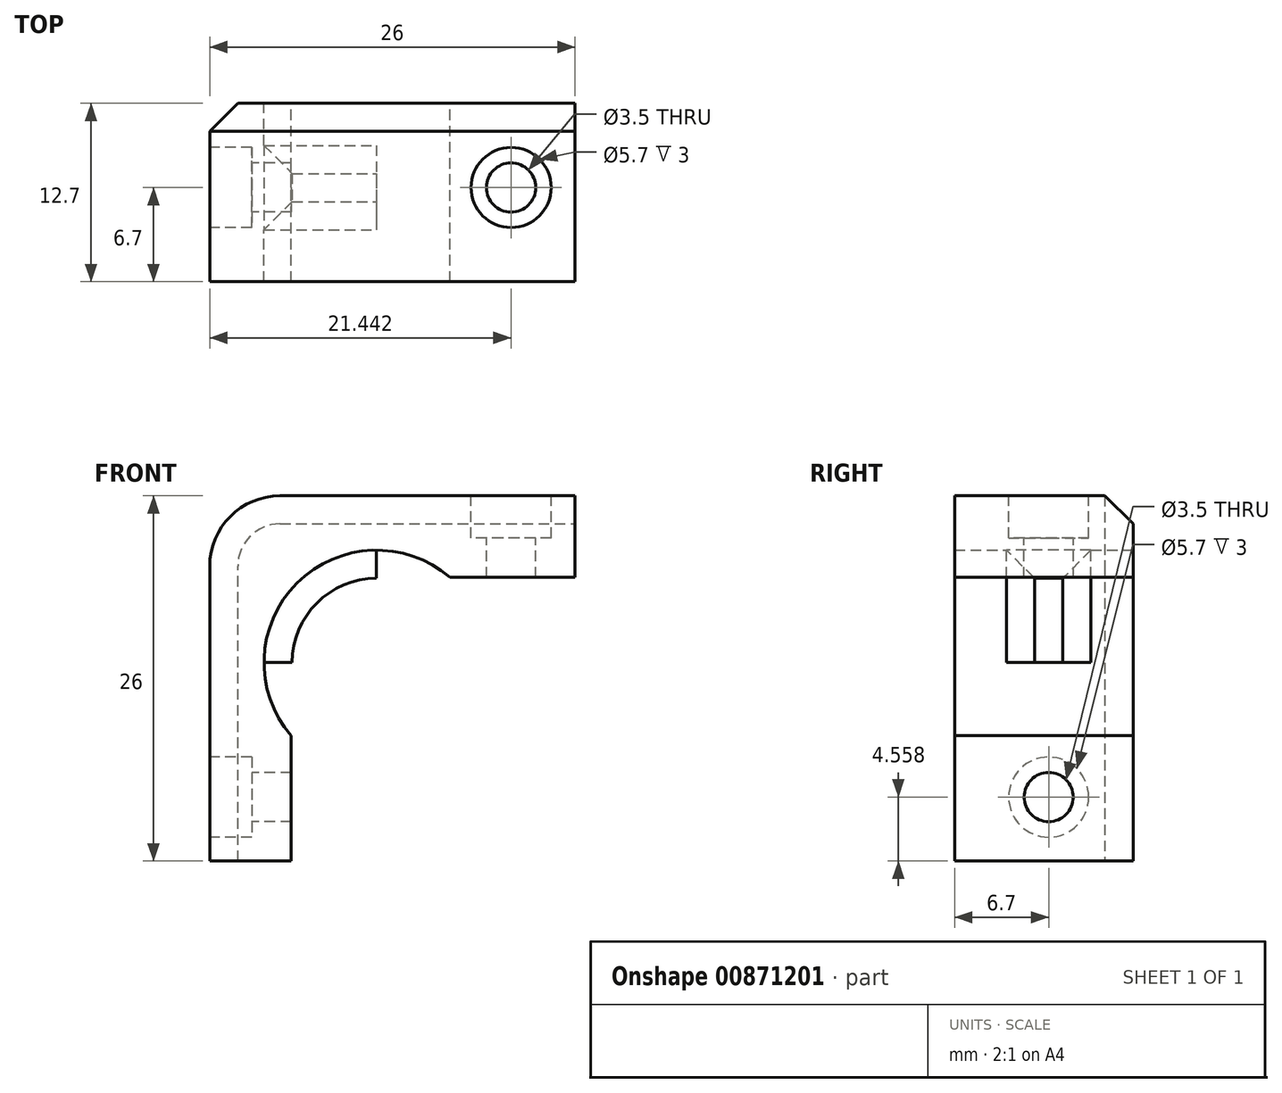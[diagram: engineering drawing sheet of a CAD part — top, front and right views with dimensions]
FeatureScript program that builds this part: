
annotation { "Feature Type Name" : "Feature", "Feature Type Description" : "" }
export const myFeature = defineFeature(function(context is Context, id is Id, definition is map)
    precondition{}
    {
        {
            var Q0;
            Q0=qCreatedBy(makeId("Front.planeOp"),FACE);
            var sketch = newSketch(context, id + "F0", { "sketchPlane" : qUnion([Q0])});
            skLineSegment(sketch, "E0", {"start": v(0, 0) * mm, "end": v(26, 0) * mm});
            skLineSegment(sketch, "E1", {"start": v(26, 0) * mm, "end": v(26, -5.8) * mm});
            skLineSegment(sketch, "E2", {"start": v(26, -5.8) * mm, "end": v(5.8, -5.8) * mm});
            skLineSegment(sketch, "E3", {"start": v(5.8, -26) * mm, "end": v(0, -26) * mm});
            skLineSegment(sketch, "E4", {"start": v(0, -26) * mm, "end": v(0, 0) * mm});
            skLineSegment(sketch, "E5.trimOffspring", {"start": v(5.8, -5.8) * mm, "end": v(5.8, -26) * mm});
            skLineSegment(sketch, "E6", {"start": v(0, 0) * mm, "end": v(27.33, -27.33) * mm, "construction": true});
            skCircle(sketch, "E7", {"center": v(11.87, -11.87) * mm, "radius": 8 * mm});
            skSolve(sketch);
        }
        {
            var Q0;
            Q0=makeQuery(id+"F0.imprint","IMPRINT",FACE,{"disambiguationData":[TD([[makeQuery(id+"F0.imprint","IMPRINT",EDGE,{"derivedFrom":sQuery(id+"F0.wireOp",EDGE,"E0")}),-1.0]])]});
            var Q1;
            {var subQ0=sQuery(id+"F0.wireOp",EDGE,"E5.trimOffspring");var subQ1=sQuery(id+"F0.wireOp",EDGE,"E2");var subQ2=makeQuery(id+"F0.imprint","INTERSECT",VERTEX,{"derivedFrom":[subQ1,subQ0]});Q1=makeQuery(id+"F0.imprint","IMPRINT",FACE,{"disambiguationData":[TD([[makeQuery(id+"F0.imprint","IMPRINT",EDGE,{"disambiguationData":[TD([[subQ2,1.0]])],"derivedFrom":subQ1}),1.0]])]});}
            extrude(context, id + "F1", {"entities" : qUnion([Q0, Q1]), "depth" : 12.7 * mm, "offsetDistance" : 25 * mm});
        }
        {
            var Q0;
            Q0=makeQuery(id+"F1.opExtrude","CAP_FACE",FACE,{"disambiguationData":[OSD([sQuery(id+"F0.wireOp",EDGE,"E0"),sQuery(id+"F0.wireOp",EDGE,"E1"),sQuery(id+"F0.wireOp",EDGE,"E2"),sQuery(id+"F0.wireOp",EDGE,"FSkOVY3p-YLGX-246F-mfNS-cTI5WIhcC46e"),sQuery(id+"F0.wireOp",EDGE,"E3"),sQuery(id+"F0.wireOp",EDGE,"E4")])],"isStart":true});
            cPlane(context, id + "F2", {"entities" : qUnion([Q0]), "cplaneType" : CPlaneType.OFFSET, "offset" : 6 * mm, "oppositeDirection" : true, "width" : 150 * mm, "height" : 150 * mm});
        }
        {
            var Q0;
            Q0=makeQuery(id+"F1.opExtrude","SWEPT_FACE",FACE,{"disambiguationData":[OSD([sQuery(id+"F0.wireOp",EDGE,"E0")])]});
            var sketch = newSketch(context, id + "F3", { "sketchPlane" : qUnion([Q0])});
            skCircle(sketch, "E8", {"center": v(21.44, -6) * mm, "radius": 1.75 * mm});
            skSolve(sketch);
        }
        {
            var Q0;
            Q0=makeQuery(id+"F3.imprint","IMPRINT",FACE,{"disambiguationData":[TD([[makeQuery(id+"F3.imprint","IMPRINT",EDGE,{"derivedFrom":sQuery(id+"F3.wireOp",EDGE,"E8")}),1.0]])]});
            extrude(context, id + "F4", {"entities" : qUnion([Q0]), "operationType" : NewBodyOperationType.REMOVE, "endBound" : BoundingType.THROUGH_ALL, "oppositeDirection" : true, "depth" : 25 * mm, "offsetDistance" : 25 * mm});
        }
        {
            var Q0;
            Q0=makeQuery(id+"F1.opExtrude","SWEPT_FACE",FACE,{"disambiguationData":[OSD([sQuery(id+"F0.wireOp",EDGE,"E4")])]});
            var sketch = newSketch(context, id + "F5", { "sketchPlane" : qUnion([Q0])});
            skCircle(sketch, "E9", {"center": v(6, -21.44) * mm, "radius": 1.75 * mm});
            skSolve(sketch);
        }
        {
            var Q0;
            Q0 = qSketchRegion(id + "F5", true);
            extrude(context, id + "F6", {"entities" : qUnion([Q0]), "operationType" : NewBodyOperationType.REMOVE, "endBound" : BoundingType.THROUGH_ALL, "oppositeDirection" : true, "depth" : 25 * mm, "offsetDistance" : 25 * mm});
        }
        {
            var Q0;
            Q0=qCreatedBy(id+"F2.planeOp",FACE);
            var sketch = newSketch(context, id + "F7", { "sketchPlane" : qUnion([Q0])});
            skArc(sketch, "E10.0", {"start": v(-17.08, -5.8) * mm, "mid": v(-6.21, -6.21) * mm, "end": v(-5.8, -17.08) * mm});
            skLineSegment(sketch, "E11", {"start": v(-11.87, -5.87) * mm, "end": v(-11.87, -3.87) * mm});
            skLineSegment(sketch, "E12", {"start": v(-5.87, -11.87) * mm, "end": v(-3.87, -11.87) * mm});
            skArc(sketch, "E13.0", {"start": v(-11.87, -5.87) * mm, "mid": v(-7.63, -7.63) * mm, "end": v(-5.87, -11.87) * mm});
            skSolve(sketch);
        }
        {
            var Q0;
            {var subQ0=sQuery(id+"F7.wireOp",EDGE,"E11");Q0=makeQuery(id+"F7.imprint","IMPRINT",FACE,{"disambiguationData":[TD([[makeQuery(id+"F7.imprint","IMPRINT",EDGE,{"derivedFrom":subQ0}),-1.0]])]});}
            extrude(context, id + "F8", {"entities" : qUnion([Q0]), "operationType" : NewBodyOperationType.ADD, "endBound" : BoundingType.SYMMETRIC, "depth" : 6 * mm, "offsetDistance" : 25 * mm});
        }
        {
            var Q0;
            Q0=makeQuery(id+"F8.opExtrude","CAP_EDGE",EDGE,{"disambiguationData":[OSD([sQuery(id+"F7.wireOp",EDGE,"E13.0")])],"isStart":true});
            var Q1;
            Q1=makeQuery(id+"F8.opExtrude","CAP_EDGE",EDGE,{"disambiguationData":[OSD([sQuery(id+"F7.wireOp",EDGE,"E13.0")])],"isStart":false});
            chamfer(context, id + "F9", {"entities" : qUnion([Q0, Q1]), "width" : 2 * mm, "tangentPropagation" : true});
        }
        {
            var Q0;
            Q0=makeQuery(id+"F1.opExtrude","SWEPT_FACE",FACE,{"disambiguationData":[OSD([sQuery(id+"F0.wireOp",EDGE,"E4")])]});
            var sketch = newSketch(context, id + "F10", { "sketchPlane" : qUnion([Q0])});
            skCircle(sketch, "E14", {"center": v(6, -21.44) * mm, "radius": 2.85 * mm});
            skSolve(sketch);
        }
        {
            var Q0;
            Q0=makeQuery(id+"F10.imprint","IMPRINT",FACE,{"disambiguationData":[TD([[makeQuery(id+"F10.imprint","IMPRINT",EDGE,{"derivedFrom":sQuery(id+"F10.wireOp",EDGE,"E14")}),1.0]])]});
            extrude(context, id + "F11", {"entities" : qUnion([Q0]), "operationType" : NewBodyOperationType.REMOVE, "oppositeDirection" : true, "depth" : 3 * mm, "offsetDistance" : 25 * mm});
        }
        {
            var Q0;
            Q0=makeQuery(id+"F1.opExtrude","SWEPT_FACE",FACE,{"disambiguationData":[OSD([sQuery(id+"F0.wireOp",EDGE,"E0")])]});
            var sketch = newSketch(context, id + "F12", { "sketchPlane" : qUnion([Q0])});
            skCircle(sketch, "E15", {"center": v(21.44, -6) * mm, "radius": 2.85 * mm});
            skSolve(sketch);
        }
        {
            var Q0;
            Q0 = qSketchRegion(id + "F12", true);
            extrude(context, id + "F13", {"entities" : qUnion([Q0]), "operationType" : NewBodyOperationType.REMOVE, "oppositeDirection" : true, "depth" : 3 * mm, "offsetDistance" : 25 * mm});
        }
        {
            var Q0;
            Q0=makeQuery(id+"F1.opExtrude","SWEPT_EDGE",EDGE,{"disambiguationData":[OSD([sQuery(id+"F0.wireOp",EDGE,"E0"),sQuery(id+"F0.wireOp",EDGE,"E4")])]});
            fillet(context, id + "F14", {"entities" : qUnion([Q0]), "radius" : 5 * mm, "tangentPropagation" : true, "allowEdgeOverflow" : false});
        }
        {
            var Q0;
            Q0=makeQuery(id+"F1.opExtrude","CAP_EDGE",EDGE,{"disambiguationData":[OSD([sQuery(id+"F0.wireOp",EDGE,"E4")])],"isStart":true});
            chamfer(context, id + "F15", {"entities" : qUnion([Q0]), "width" : 2 * mm, "tangentPropagation" : true});
        }
    });
